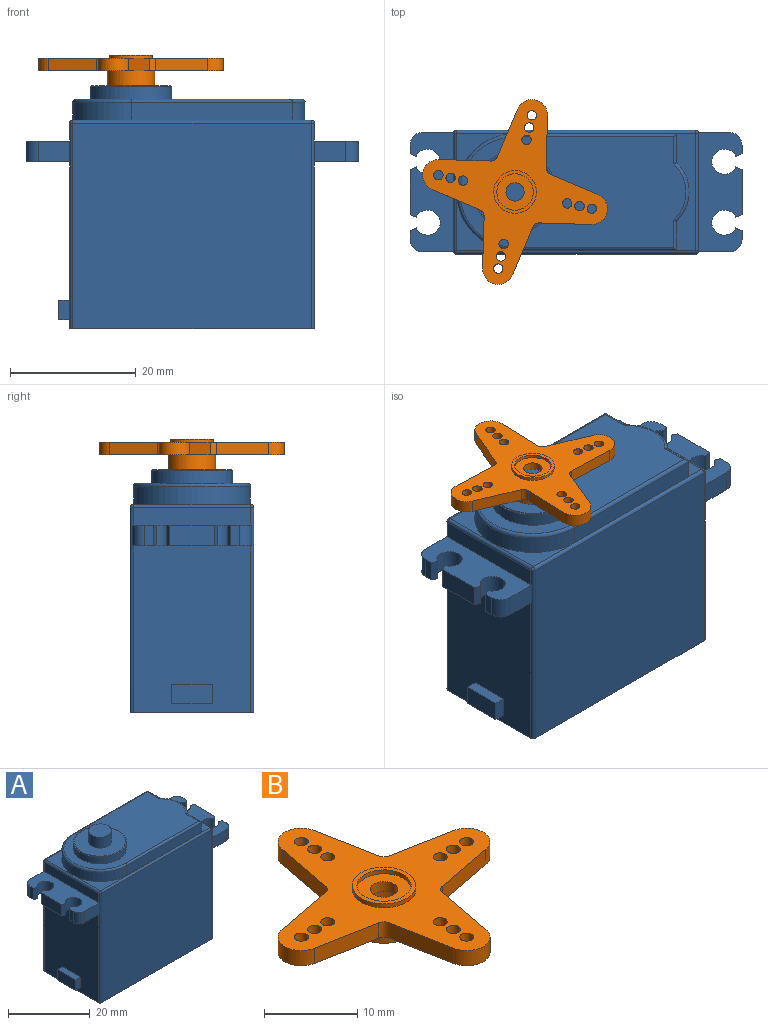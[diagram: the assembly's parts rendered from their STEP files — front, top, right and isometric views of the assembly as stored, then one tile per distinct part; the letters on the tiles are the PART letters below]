
ASSEMBLY  parts=2 mates=1
PART A: 74 faces, bbox 52.9x20.1x41.9 mm
  f0: plane 26.56x18.7mm, normal (-1,0,0), area 476.5mm2, adj f4,f24,f59,f61,f69,f70,f71,f72
  f1: plane 18.7x2.8mm, normal (1,0,0), area 52.4mm2, adj f17,f51,f55,f57
  f2: plane 38x18.7mm, normal (0,0,1), area 83.8mm2, adj f34,f35,f36,f37,f38,f39,f51,f52
  f3: plane 18.7x2.8mm, normal (-1,0,0), area 52.4mm2, adj f23,f54,f59,f61
  f4: plane 39x19.7mm, normal (0,0,-1), area 768.1mm2, adj f0,f5,f6,f7,f55,f57,f59,f61
  f5: plane 26.56x18.7mm, normal (1,0,0), area 496.7mm2, adj f4,f18,f55,f57
  f6: plane 38x32.7mm, normal (0,-1,0), area 1242.6mm2, adj f4,f52,f55,f59
  f7: plane 38x32.7mm, normal (0,1,0), area 1242.6mm2, adj f4,f53,f57,f61
  f8: plane 3.34x1.38mm, normal (1,0,0), area 4.6mm2, adj f9,f17,f18,f48
  f9: plane 3.34x0.98mm, normal (0.41,0.91,0), area 3.6mm2, adj f8,f10,f17,f18
  f10: cylinder r=2mm len=4mm, axis (0,0,-1), area 36.3mm2, adj f9,f11,f17,f18
  f11: plane 3.34x0.98mm, normal (0.41,-0.91,0), area 3.6mm2, adj f10,f12,f17,f18
  f12: plane 7.16x3.34mm, normal (1,0,0), area 23.9mm2, adj f11,f13,f17,f18
  f13: plane 3.34x0.98mm, normal (0.41,0.91,0), area 3.6mm2, adj f12,f14,f17,f18
  f14: cylinder r=2mm len=4mm, axis (0,0,-1), area 36.3mm2, adj f13,f15,f17,f18
  f15: plane 3.34x0.98mm, normal (0.41,-0.91,0), area 3.6mm2, adj f14,f16,f17,f18
  f16: plane 3.34x1.38mm, normal (1,0,0), area 4.6mm2, adj f15,f17,f18,f49
  f17: plane 19x6.95mm, normal (0,0,1), area 101.1mm2, adj f1,f8,f9,f10,f11,f12,f13,f14
  f18: plane 19x6.95mm, normal (0,0,-1), area 101.1mm2, adj f5,f8,f9,f10,f11,f12,f13,f14
  f19: plane 4.95x3.34mm, normal (0,1,0), area 16.5mm2, adj f17,f18,f49,f57
  f20: plane 4.95x3.34mm, normal (0,-1,0), area 16.5mm2, adj f17,f18,f48,f55
  f21: plane 4.95x3.34mm, normal (0,-1,0), area 16.5mm2, adj f23,f24,f47,f59
  f22: plane 4.95x3.34mm, normal (0,1,0), area 16.5mm2, adj f23,f24,f50,f61
  f23: plane 19x6.95mm, normal (0,0,1), area 101.1mm2, adj f3,f21,f22,f25,f26,f27,f28,f29
  f24: plane 19x6.95mm, normal (0,0,-1), area 101.1mm2, adj f0,f21,f22,f25,f26,f27,f28,f29
  f25: cylinder r=2mm len=4mm, axis (0,0,-1), area 36.3mm2, adj f23,f24,f26,f33
  f26: plane 3.34x0.98mm, normal (-0.41,0.91,0), area 3.6mm2, adj f23,f24,f25,f27
  f27: plane 3.34x1.38mm, normal (-1,0,0), area 4.6mm2, adj f23,f24,f26,f47
  f28: plane 3.34x1.38mm, normal (-1,0,0), area 4.6mm2, adj f23,f24,f29,f50
  f29: plane 3.34x0.98mm, normal (-0.41,-0.91,0), area 3.6mm2, adj f23,f24,f28,f30
  f30: cylinder r=2mm len=4mm, axis (0,0,-1), area 36.3mm2, adj f23,f24,f29,f31
  f31: plane 3.34x0.98mm, normal (-0.41,0.91,0), area 3.6mm2, adj f23,f24,f30,f32
  f32: plane 7.16x3.34mm, normal (-1,0,0), area 23.9mm2, adj f23,f24,f31,f33
  f33: plane 3.34x0.98mm, normal (-0.41,-0.91,0), area 3.6mm2, adj f23,f24,f25,f32
  f34: cylinder r=9.3mm len=18.6mm, axis (0,0,-1), area 83mm2, adj f2,f35,f39,f65
  f35: plane 25.7x2.84mm, normal (0,-1,0), area 73mm2, adj f2,f34,f36,f63
  f36: plane 4.61x2.84mm, normal (1,0,0), area 13.1mm2, adj f2,f35,f37,f64
  f37: cylinder r=6.5mm len=9.38mm, axis (0,0,-1), area 29.8mm2, adj f2,f36,f38,f66
  f38: plane 4.61x2.84mm, normal (1,0,0), area 13.1mm2, adj f2,f37,f39,f68
  f39: plane 25.7x2.84mm, normal (0,1,0), area 73mm2, adj f2,f34,f38,f67
  f40: plane 36x17.6mm, normal (0,0,1), area 444.8mm2, adj f41,f63,f64,f65,f66,f67,f68
  f41: cylinder r=6.5mm len=13mm, axis (0,0,-1), area 81.7mm2, adj f40,f42
  f42: plane 13x13mm, normal (0,0,1), area 10mm2, adj f41,f43
  f43: cylinder r=6.25mm len=12.5mm, axis (0,0,-1), area 4.7mm2, adj f42,f44
  f44: plane 12.5x12.5mm, normal (0,0,1), area 97.6mm2, adj f43,f45
  f45: cylinder r=2.82mm len=5.65mm, axis (0,0,-1), area 57.7mm2, adj f44,f46
  f46: plane 5.65x5.65mm, normal (0,0,1), area 25.1mm2, adj f45
  f47: cylinder r=2mm len=3.34mm, axis (0,0,1), area 10.5mm2, adj f21,f23,f24,f27
  f48: cylinder r=2mm len=3.34mm, axis (0,0,-1), area 10.5mm2, adj f8,f17,f18,f20
  f49: cylinder r=2mm len=3.34mm, axis (0,0,1), area 10.5mm2, adj f16,f17,f18,f19
  f50: cylinder r=2mm len=3.34mm, axis (0,0,-1), area 10.5mm2, adj f22,f23,f24,f28
  f51: cylinder r=0.5mm len=18.7mm, axis (0,1,0), area 14.7mm2, adj f1,f2,f56,f58
  f52: cylinder r=0.5mm len=38mm, axis (1,0,0), area 29.8mm2, adj f2,f6,f56,f60
  f53: cylinder r=0.5mm len=38mm, axis (-1,0,0), area 29.8mm2, adj f2,f7,f58,f62
  f54: cylinder r=0.5mm len=18.7mm, axis (0,-1,0), area 14.7mm2, adj f2,f3,f60,f62
  f55: cylinder r=0.5mm len=32.7mm, axis (0,0,-1), area 25.2mm2, adj f1,f4,f5,f6,f17,f18,f20,f56
  f56: sphere r=0.5mm, area 0.4mm2, adj f51,f52,f55
  f57: cylinder r=0.5mm len=32.7mm, axis (0,0,1), area 25.2mm2, adj f1,f4,f5,f7,f17,f18,f19,f58
  f58: sphere r=0.5mm, area 0.4mm2, adj f51,f53,f57
  f59: cylinder r=0.5mm len=32.7mm, axis (0,0,1), area 25.2mm2, adj f0,f3,f4,f6,f21,f23,f24,f60
  f60: sphere r=0.5mm, area 0.4mm2, adj f52,f54,f59
  f61: cylinder r=0.5mm len=32.7mm, axis (0,0,-1), area 25.2mm2, adj f0,f3,f4,f7,f22,f23,f24,f62
  f62: sphere r=0.5mm, area 0.4mm2, adj f53,f54,f61
  f63: cylinder r=0.5mm len=25.7mm, axis (-1,0,0), area 20mm2, adj f35,f40,f64,f65
  f64: cylinder r=0.5mm len=4.83mm, axis (0,-1,0), area 3.5mm2, adj f36,f40,f63,f66
  f65: torus R=8.8mm, axis (0,0,1), area 22.5mm2, adj f34,f40,f63,f67
  f66: torus R=6mm, axis (0,0,1), area 8.1mm2, adj f37,f40,f64,f68
  f67: cylinder r=0.5mm len=25.7mm, axis (1,0,0), area 20mm2, adj f39,f40,f65,f68
  f68: cylinder r=0.5mm len=4.83mm, axis (0,-1,0), area 3.5mm2, adj f38,f40,f66,f67
  f69: plane 6.4x1.75mm, normal (0,0,-1), area 11.2mm2, adj f0,f70,f72,f73
  f70: plane 3.15x1.75mm, normal (0,-1,0), area 5.5mm2, adj f0,f69,f71,f73
  f71: plane 6.4x1.75mm, normal (0,0,1), area 11.2mm2, adj f0,f70,f72,f73
  f72: plane 3.15x1.75mm, normal (0,1,0), area 5.5mm2, adj f0,f69,f71,f73
  f73: plane 6.4x3.15mm, normal (-1,0,0), area 20.2mm2, adj f69,f70,f71,f72
PART B: 39 faces, bbox 30x30x4.9 mm
  f0: cylinder r=2.5mm len=4.91mm, axis (0,0,-1), area 13.8mm2, adj f1,f27,f28,f29
  f1: plane 8.17x2mm, normal (0.98,-0.18,0), area 16.6mm2, adj f0,f2,f28,f29
  f2: cylinder r=1mm len=2mm, axis (0,0,-1), area 2.4mm2, adj f1,f3,f28,f29
  f3: plane 8.17x2mm, normal (0.18,-0.98,0), area 16.6mm2, adj f2,f4,f28,f29
  f4: cylinder r=2.5mm len=4.91mm, axis (0,0,-1), area 13.8mm2, adj f3,f5,f28,f29
  f5: plane 8.17x2mm, normal (0.18,0.98,0), area 16.6mm2, adj f4,f6,f28,f29
  f6: cylinder r=1mm len=2mm, axis (0,0,-1), area 2.4mm2, adj f5,f7,f28,f29
  f7: plane 8.17x2mm, normal (0.98,0.18,0), area 16.6mm2, adj f6,f8,f28,f29
  f8: cylinder r=2.5mm len=4.91mm, axis (0,0,-1), area 13.8mm2, adj f7,f9,f28,f29
  f9: plane 8.17x2mm, normal (-0.98,0.18,0), area 16.6mm2, adj f8,f10,f28,f29
  f10: cylinder r=1mm len=2mm, axis (0,0,-1), area 2.4mm2, adj f9,f11,f28,f29
  f11: plane 8.17x2mm, normal (-0.18,0.98,0), area 16.6mm2, adj f10,f12,f28,f29
  f12: cylinder r=2.5mm len=4.91mm, axis (0,0,-1), area 13.8mm2, adj f11,f13,f28,f29
  f13: plane 8.17x2mm, normal (-0.18,-0.98,0), area 16.6mm2, adj f12,f14,f28,f29
  f14: cylinder r=1mm len=2mm, axis (0,0,-1), area 2.4mm2, adj f13,f27,f28,f29
  f15: cylinder r=0.75mm len=2mm, axis (0,0,-1), area 9.4mm2, adj f28,f29
  f16: cylinder r=0.75mm len=2mm, axis (0,0,-1), area 9.4mm2, adj f28,f29
  f17: cylinder r=0.75mm len=2mm, axis (0,0,-1), area 9.4mm2, adj f28,f29
  f18: cylinder r=0.75mm len=2mm, axis (0,0,-1), area 9.4mm2, adj f28,f29
  f19: cylinder r=0.75mm len=2mm, axis (0,0,-1), area 9.4mm2, adj f28,f29
  f20: cylinder r=0.75mm len=2mm, axis (0,0,-1), area 9.4mm2, adj f28,f29
  f21: cylinder r=0.75mm len=2mm, axis (0,0,-1), area 9.4mm2, adj f28,f29
  f22: cylinder r=0.75mm len=2mm, axis (0,0,-1), area 9.4mm2, adj f28,f29
  f23: cylinder r=0.75mm len=2mm, axis (0,0,-1), area 9.4mm2, adj f28,f29
  f24: cylinder r=0.75mm len=2mm, axis (0,0,-1), area 9.4mm2, adj f28,f29
  f25: cylinder r=0.75mm len=2mm, axis (0,0,-1), area 9.4mm2, adj f28,f29
  f26: cylinder r=0.75mm len=2mm, axis (0,0,-1), area 9.4mm2, adj f28,f29
  f27: plane 8.17x2mm, normal (-0.98,-0.18,0), area 16.6mm2, adj f0,f14,f28,f29
  f28: plane 30x30mm, normal (0,0,1), area 273.4mm2, adj f0,f1,f2,f3,f4,f5,f6,f7
  f29: plane 30x30mm, normal (0,0,-1), area 265.3mm2, adj f0,f1,f2,f3,f4,f5,f6,f7
  f30: cylinder r=2.9mm len=5.8mm, axis (0,0,-1), area 9.1mm2, adj f32,f33
  f31: cylinder r=3.4mm len=6.8mm, axis (0,0,-1), area 10.7mm2, adj f28,f32
  f32: plane 6.8x6.8mm, normal (0,0,1), area 9.9mm2, adj f30,f31
  f33: plane 5.8x5.8mm, normal (0,0,1), area 19.8mm2, adj f30,f38
  f34: cylinder r=3.76mm len=7.52mm, axis (0,0,1), area 56.7mm2, adj f29,f35
  f35: plane 7.52x7.52mm, normal (0,0,-1), area 17.1mm2, adj f34,f36
  f36: cylinder r=2.95mm len=5.9mm, axis (0,0,-1), area 57.5mm2, adj f35,f37
  f37: plane 5.9x5.9mm, normal (0,0,-1), area 20.7mm2, adj f36,f38
  f38: cylinder r=1.45mm len=2.9mm, axis (0,0,-1), area 11.8mm2, adj f33,f37
PLACE A t=(-5.72,-0.72,1.08)mm fixed
PLACE B rot(axis=(0,0,-1),12.4deg) t=(-5.72,-0.72,15.58)mm
MATE revolute B.f36 <-> A.f45  axis (0,0,-1) through (-5.72,-0.72,13.18)mm
